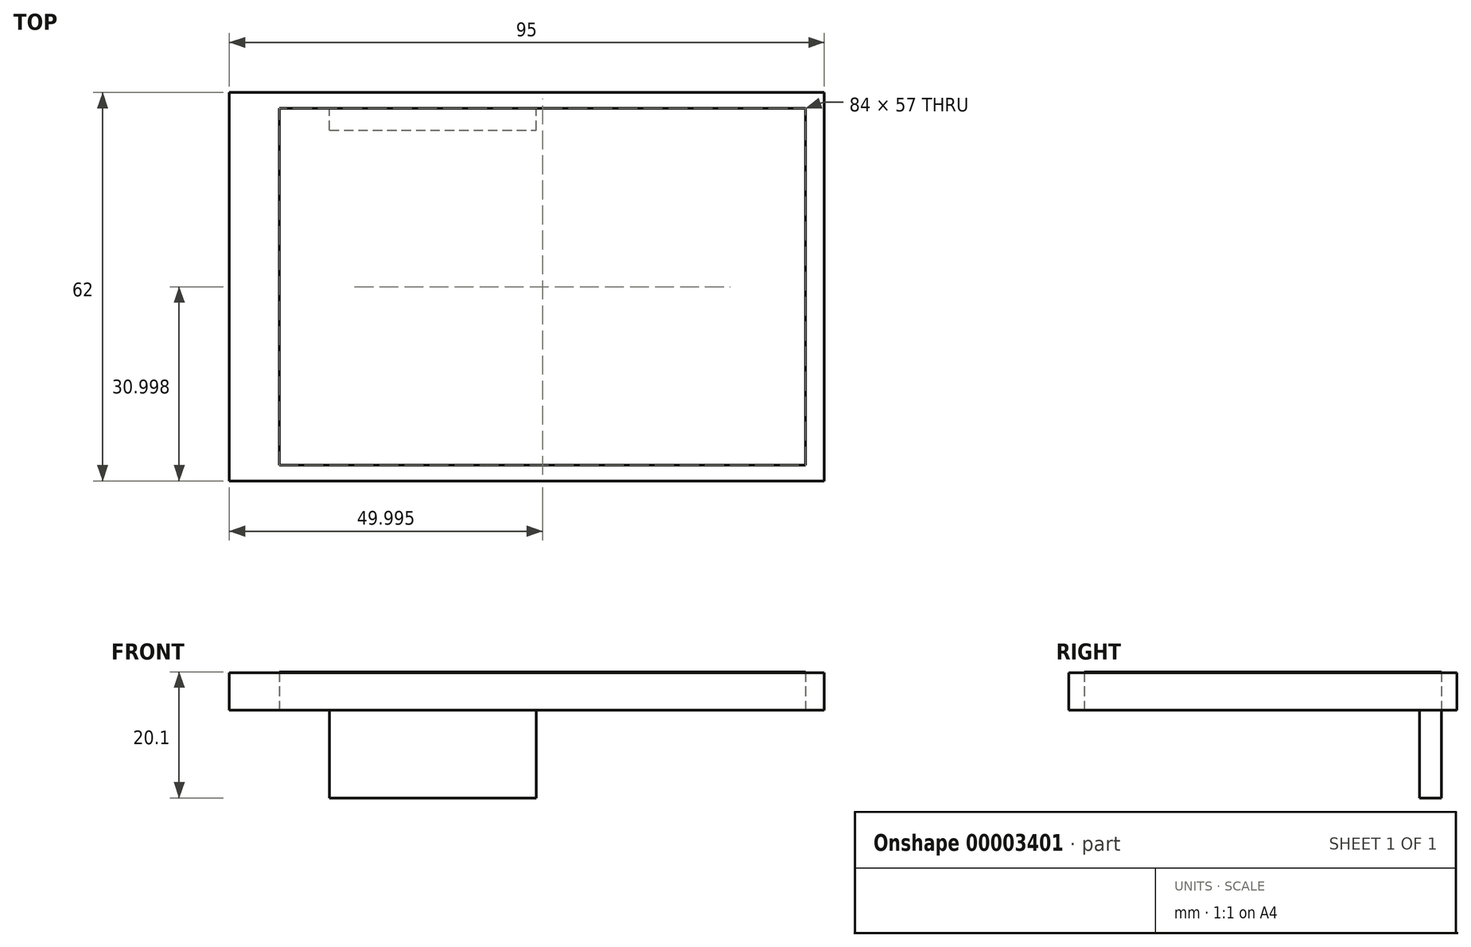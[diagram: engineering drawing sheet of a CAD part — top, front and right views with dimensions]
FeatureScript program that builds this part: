
annotation { "Feature Type Name" : "Feature", "Feature Type Description" : "" }
export const myFeature = defineFeature(function(context is Context, id is Id, definition is map)
    precondition{}
    {
        {
            var Q0;
            Q0=qCreatedBy(makeId("Top.planeOp"),FACE);
            var sketch = newSketch(context, id + "F0", { "sketchPlane" : qUnion([Q0])});
            skLineSegment(sketch, "E0.bottom", {"start": v(-79.85, -0.55) * mm, "end": v(15.15, -0.55) * mm});
            skLineSegment(sketch, "E0.top", {"start": v(-79.85, -62.55) * mm, "end": v(15.15, -62.55) * mm});
            skLineSegment(sketch, "E0.left", {"start": v(-79.85, -0.55) * mm, "end": v(-79.85, -62.55) * mm});
            skLineSegment(sketch, "E0.right", {"start": v(15.15, -0.55) * mm, "end": v(15.15, -62.55) * mm});
            skLineSegment(sketch, "E1.bottom", {"start": v(-71.85, -3.05) * mm, "end": v(12.15, -3.05) * mm});
            skLineSegment(sketch, "E1.top", {"start": v(-71.85, -60.05) * mm, "end": v(12.15, -60.05) * mm});
            skLineSegment(sketch, "E1.left", {"start": v(-71.85, -3.05) * mm, "end": v(-71.85, -60.05) * mm});
            skLineSegment(sketch, "E1.right", {"start": v(12.15, -3.05) * mm, "end": v(12.15, -60.05) * mm});
            skSolve(sketch);
        }
        {
            var Q0;
            Q0=makeQuery(id+"F0.imprint","IMPRINT",FACE,{"disambiguationData":[TD([[makeQuery(id+"F0.imprint","IMPRINT",EDGE,{"derivedFrom":sQuery(id+"F0.wireOp",EDGE,"E0.bottom")}),-1.0]])]});
            extrude(context, id + "F1", {"entities" : qUnion([Q0]), "depth" : 6 * mm});
        }
        {
            var Q0;
            Q0=makeQuery(id+"F1.opExtrude","CAP_FACE",FACE,{"disambiguationData":[OSD([sQuery(id+"F0.wireOp",EDGE,"E0.bottom"),sQuery(id+"F0.wireOp",EDGE,"E0.top"),sQuery(id+"F0.wireOp",EDGE,"E0.left"),sQuery(id+"F0.wireOp",EDGE,"E0.right"),sQuery(id+"F0.wireOp",EDGE,"E1.bottom"),sQuery(id+"F0.wireOp",EDGE,"E1.top"),sQuery(id+"F0.wireOp",EDGE,"E1.left"),sQuery(id+"F0.wireOp",EDGE,"E1.right")])],"isStart":true});
            var sketch = newSketch(context, id + "F2", { "sketchPlane" : qUnion([Q0])});
            skLineSegment(sketch, "E2.bottom", {"start": v(-63.85, 6.55) * mm, "end": v(-30.85, 6.55) * mm});
            skLineSegment(sketch, "E2.top", {"start": v(-63.85, 1.55) * mm, "end": v(-30.85, 1.55) * mm});
            skLineSegment(sketch, "E2.left", {"start": v(-63.85, 6.55) * mm, "end": v(-63.85, 1.55) * mm});
            skLineSegment(sketch, "E2.right", {"start": v(-30.85, 6.55) * mm, "end": v(-30.85, 1.55) * mm});
            skSolve(sketch);
        }
        {
            var Q0;
            {var subQ5=sQuery(id+"F2.wireOp",EDGE,"E2.bottom");Q0=makeQuery(id+"F2.imprint","IMPRINT",FACE,{"disambiguationData":[TD([[makeQuery(id+"F2.imprint","IMPRINT",EDGE,{"derivedFrom":subQ5}),-1.0]])]});}
            extrude(context, id + "F3", {"entities" : qUnion([Q0]), "operationType" : NewBodyOperationType.ADD, "depth" : 14 * mm});
        }
        {
            var Q0;
            Q0=makeQuery(id+"F0.imprint","IMPRINT",FACE,{"disambiguationData":[TD([[makeQuery(id+"F0.imprint","IMPRINT",EDGE,{"derivedFrom":sQuery(id+"F0.wireOp",EDGE,"E1.bottom")}),-1.0]])]});
            extrude(context, id + "F4", {"entities" : qUnion([Q0]), "depth" : 6.1 * mm});
        }
    });
